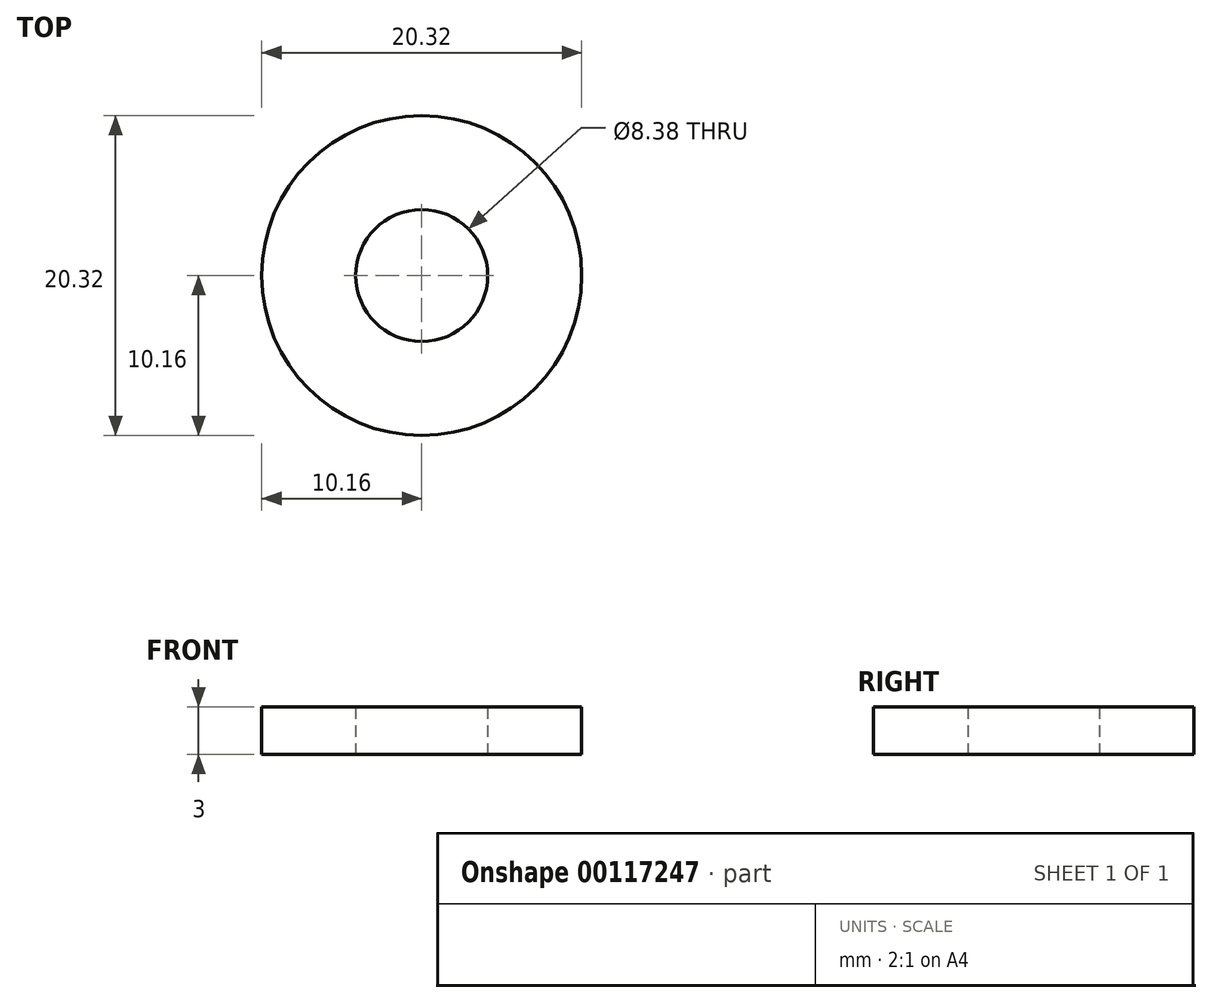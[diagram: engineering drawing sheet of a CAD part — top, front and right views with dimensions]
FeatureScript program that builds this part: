
annotation { "Feature Type Name" : "Feature", "Feature Type Description" : "" }
export const myFeature = defineFeature(function(context is Context, id is Id, definition is map)
    precondition{}
    {
        {
            var Q0;
            Q0=qCreatedBy(makeId("Top.planeOp"),FACE);
            var sketch = newSketch(context, id + "F0", { "sketchPlane" : qUnion([Q0])});
            skCircle(sketch, "E0", {"center": v(0, 0) * mm, "radius": 10.16 * mm});
            skCircle(sketch, "E1", {"center": v(0, 0) * mm, "radius": 4.2 * mm});
            skSolve(sketch);
        }
        {
            var Q0;
            Q0 = qSketchRegion(id + "F0", true);
            extrude(context, id + "F1", {"entities" : qUnion([Q0]), "depth" : 3 * mm});
        }
    });
